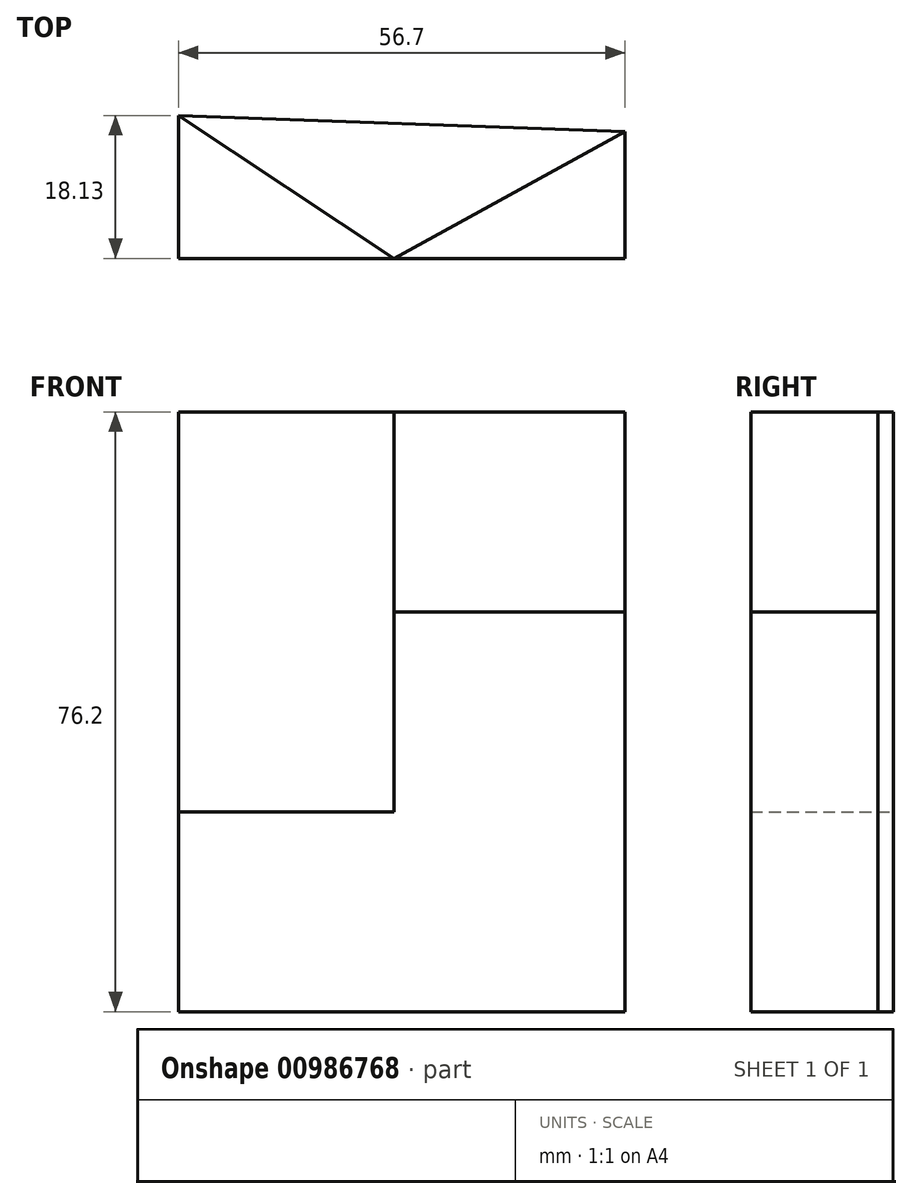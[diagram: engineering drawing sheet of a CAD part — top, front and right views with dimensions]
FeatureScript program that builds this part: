
annotation { "Feature Type Name" : "Feature", "Feature Type Description" : "" }
export const myFeature = defineFeature(function(context is Context, id is Id, definition is map)
    precondition{}
    {
        {
            var Q0;
            Q0=qCreatedBy(makeId("Top.planeOp"),FACE);
            var sketch = newSketch(context, id + "F0", { "sketchPlane" : qUnion([Q0])});
            skLineSegment(sketch, "E0", {"start": v(-39.29, 24.9) * mm, "end": v(-11.94, 24.9) * mm});
            skLineSegment(sketch, "E1", {"start": v(-39.29, 24.9) * mm, "end": v(-39.29, 43.03) * mm});
            skLineSegment(sketch, "E2", {"start": v(-39.29, 43.03) * mm, "end": v(-11.94, 24.9) * mm});
            skLineSegment(sketch, "E3", {"start": v(-11.94, 24.9) * mm, "end": v(17.41, 24.9) * mm});
            skLineSegment(sketch, "E4", {"start": v(17.41, 24.9) * mm, "end": v(17.41, 41.01) * mm});
            skLineSegment(sketch, "E5", {"start": v(17.41, 41.01) * mm, "end": v(-11.94, 24.9) * mm});
            skLineSegment(sketch, "E6", {"start": v(17.41, 41.01) * mm, "end": v(-39.29, 43.03) * mm});
            skSolve(sketch);
        }
        {
            var Q0;
            Q0=makeQuery(id+"F0.imprint","IMPRINT",FACE,{"disambiguationData":[TD([[makeQuery(id+"F0.imprint","IMPRINT",EDGE,{"derivedFrom":sQuery(id+"F0.wireOp",EDGE,"E0")}),1.0]])]});
            extrude(context, id + "F1", {"entities" : qUnion([Q0]), "depth" : 25.4 * mm, "offsetDistance" : 25.4 * mm});
        }
        {
            var Q0;
            Q0=makeQuery(id+"F0.imprint","IMPRINT",FACE,{"disambiguationData":[TD([[makeQuery(id+"F0.imprint","IMPRINT",EDGE,{"derivedFrom":sQuery(id+"F0.wireOp",EDGE,"E2")}),1.0]])]});
            extrude(context, id + "F2", {"entities" : qUnion([Q0]), "operationType" : NewBodyOperationType.ADD, "depth" : 76.2 * mm, "offsetDistance" : 25.4 * mm});
        }
        {
            var Q0;
            Q0=makeQuery(id+"F0.imprint","IMPRINT",FACE,{"disambiguationData":[TD([[makeQuery(id+"F0.imprint","IMPRINT",EDGE,{"derivedFrom":sQuery(id+"F0.wireOp",EDGE,"E3")}),1.0]])]});
            extrude(context, id + "F3", {"entities" : qUnion([Q0]), "operationType" : NewBodyOperationType.ADD, "depth" : 50.8 * mm, "offsetDistance" : 25.4 * mm});
        }
    });
